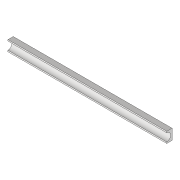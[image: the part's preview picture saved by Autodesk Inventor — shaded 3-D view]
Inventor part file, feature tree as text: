
AUTODESK INVENTOR PART (.ipt)
format: ipt  version: 2020 (Build 240168000, 168)  size: 80,896 bytes
history: native  units: mm
features: extrude x1, sketch x1
ambient origin geometry x8: Origin, YZ Plane, XZ Plane, XY Plane, X Axis, Y Axis, Z Axis, Center Point
bodies: Volumenkörper1 (feature_tree)
feature tree (2):
  extrude  "Extrusion1"  Depth=7.5mm
  sketch  "Skizze1"  dims[d0=20.0mm d1=7.5mm d2=10.0mm d3=300.0mm d4=0.0mm]
